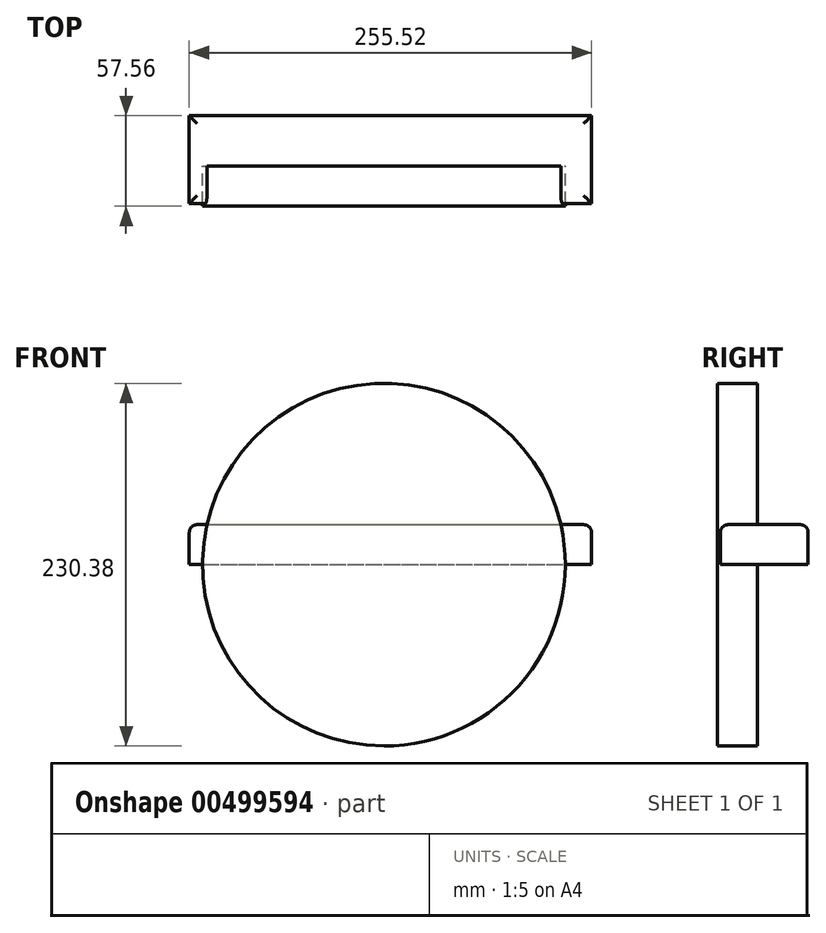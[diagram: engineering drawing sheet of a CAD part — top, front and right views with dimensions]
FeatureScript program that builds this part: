
annotation { "Feature Type Name" : "Feature", "Feature Type Description" : "" }
export const myFeature = defineFeature(function(context is Context, id is Id, definition is map)
    precondition{}
    {
        {
            var Q0;
            Q0=qCreatedBy(makeId("Top.planeOp"),FACE);
            var sketch = newSketch(context, id + "F0", { "sketchPlane" : qUnion([Q0])});
            skLineSegment(sketch, "E0.bottom", {"start": v(-123.63, -23.68) * mm, "end": v(131.9, -23.68) * mm});
            skLineSegment(sketch, "E0.top", {"start": v(-123.63, 32.16) * mm, "end": v(131.9, 32.16) * mm});
            skLineSegment(sketch, "E0.left", {"start": v(-123.63, -23.68) * mm, "end": v(-123.63, 32.16) * mm});
            skLineSegment(sketch, "E0.right", {"start": v(131.9, -23.68) * mm, "end": v(131.9, 32.16) * mm});
            skCircle(sketch, "E1.cCircle", {"center": v(0, 56.79) * mm, "radius": 158.8 * mm, "construction": true});
            skLineSegment(sketch, "E1.0", {"start": v(166.2, 72.66) * mm, "end": v(143.8, -28.07) * mm});
            skLineSegment(sketch, "E1.1", {"start": v(143.8, -28.07) * mm, "end": v(66.45, -96.38) * mm});
            skLineSegment(sketch, "E1.2", {"start": v(66.45, -96.38) * mm, "end": v(-36.27, -106.19) * mm});
            skLineSegment(sketch, "E1.3", {"start": v(-36.27, -106.19) * mm, "end": v(-125.14, -53.74) * mm});
            skLineSegment(sketch, "E1.4", {"start": v(-125.14, -53.74) * mm, "end": v(-166.2, 40.92) * mm});
            skLineSegment(sketch, "E1.5", {"start": v(-166.2, 40.92) * mm, "end": v(-143.8, 141.64) * mm});
            skLineSegment(sketch, "E1.6", {"start": v(-143.8, 141.64) * mm, "end": v(-66.45, 209.96) * mm});
            skLineSegment(sketch, "E1.7", {"start": v(-66.45, 209.96) * mm, "end": v(36.27, 219.77) * mm});
            skLineSegment(sketch, "E1.8", {"start": v(36.27, 219.77) * mm, "end": v(125.14, 167.32) * mm});
            skLineSegment(sketch, "E1.9", {"start": v(125.14, 167.32) * mm, "end": v(166.2, 72.66) * mm});
            skPoint(sketch, "E1.0.midPoint", {"position": v(155, 22.3) * mm});
            skSolve(sketch);
        }
        {
            var Q0;
            Q0=makeQuery(id+"F0.imprint","IMPRINT",FACE,{"disambiguationData":[TD([[makeQuery(id+"F0.imprint","IMPRINT",EDGE,{"derivedFrom":sQuery(id+"F0.wireOp",EDGE,"E0.bottom")}),1.0]])]});
            extrude(context, id + "F1", {"entities" : qUnion([Q0]), "depth" : 25.4 * mm});
        }
        {
            var Q0;
            Q0=makeQuery(id+"F1.opExtrude","CAP_FACE",FACE,{"disambiguationData":[OSD([sQuery(id+"F0.wireOp",EDGE,"E0.bottom"),sQuery(id+"F0.wireOp",EDGE,"E0.top"),sQuery(id+"F0.wireOp",EDGE,"E0.left"),sQuery(id+"F0.wireOp",EDGE,"E0.right")])],"isStart":false});
            fillet(context, id + "F2", {"entities" : qUnion([Q0]), "radius" : 5.08 * mm, "tangentPropagation" : true, "allowEdgeOverflow" : false});
        }
        {
            var Q0;
            Q0=qCreatedBy(makeId("Front.planeOp"),FACE);
            var sketch = newSketch(context, id + "F3", { "sketchPlane" : qUnion([Q0])});
            skCircle(sketch, "E2", {"center": v(0, 0) * mm, "radius": 115.2 * mm});
            skSolve(sketch);
        }
        {
            var Q0;
            Q0=makeQuery(id+"F3.imprint","IMPRINT",FACE,{"disambiguationData":[TD([[makeQuery(id+"F3.imprint","IMPRINT",EDGE,{"derivedFrom":sQuery(id+"F3.wireOp",EDGE,"E2")}),1.0]])]});
            extrude(context, id + "F4", {"entities" : qUnion([Q0]), "operationType" : NewBodyOperationType.ADD, "depth" : 25.4 * mm});
        }
    });
